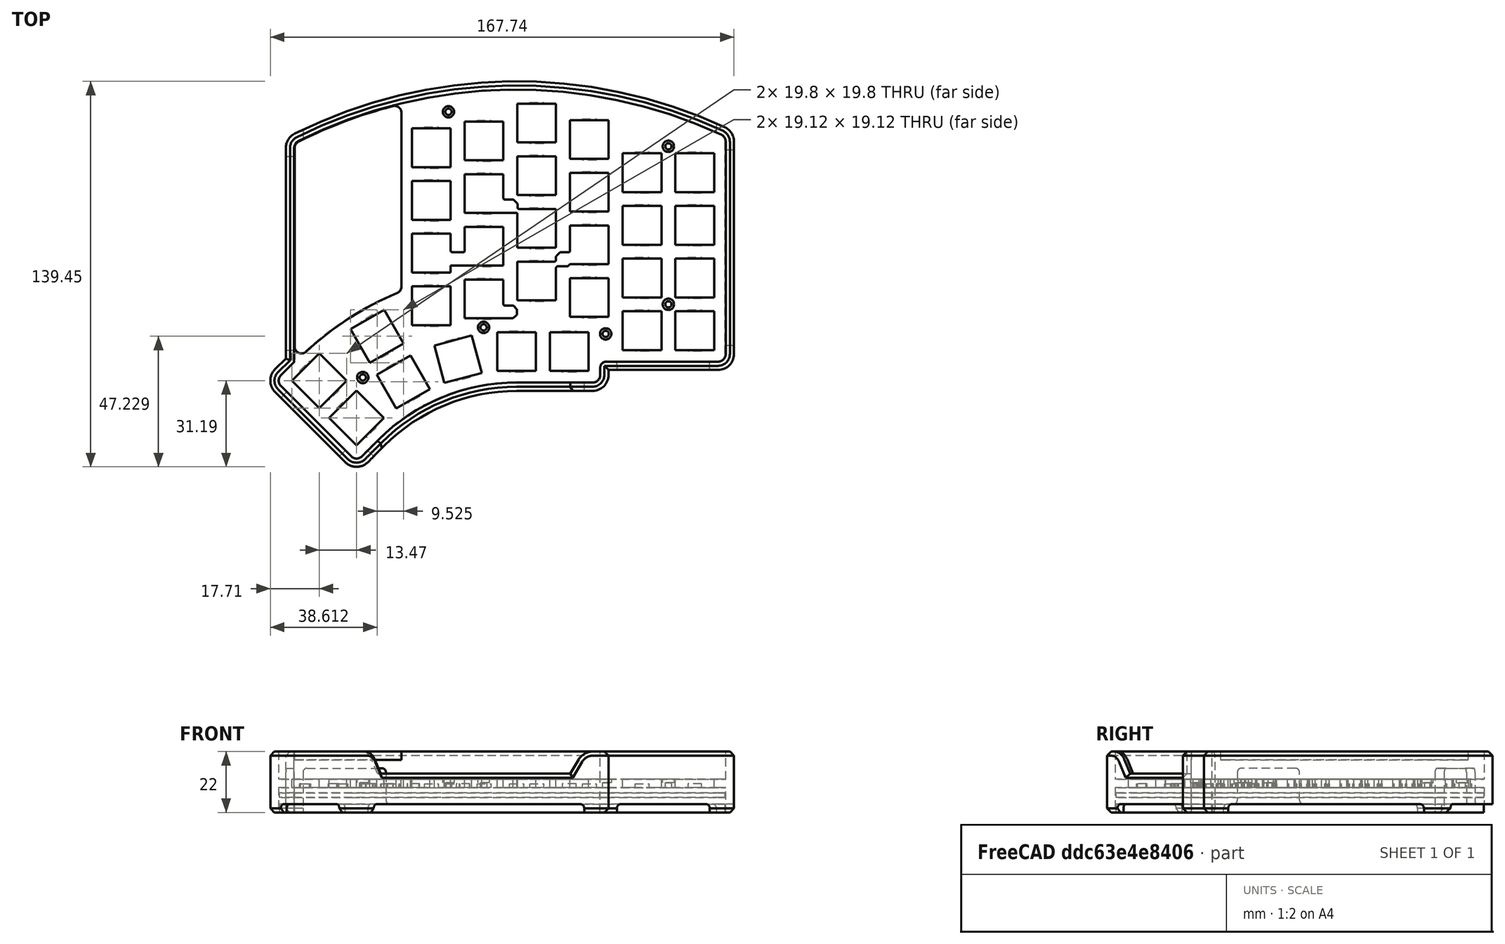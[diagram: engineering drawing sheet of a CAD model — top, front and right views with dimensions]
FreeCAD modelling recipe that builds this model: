
FCSTD DOCUMENT  (FreeCAD 1.1R38728 (Git))
Label: Elora3DPrintedCase
License: All rights reserved
LicenseURL: https://en.wikipedia.org/wiki/All_rights_reserved
objects: Sketcher::SketchObject×15, PartDesign::Pocket×12, PartDesign::Pad×7, Part::Feature×4, PartDesign::SubShapeBinder×4, PartDesign::Body×4, Part::Part2DObjectPython×1, Mesh::Feature×1, PartDesign::Chamfer×1
note: 103 computed .brp shape members not serialized (recipe doc carries the construction recipe); baked Part::Feature solids carry a one-line shape summary decoded from their .brp

FEATURE [Part::Feature] Polyline  label="Bottom Plate  - Shape"
  shape: bbox 161.3 x 133 x 2e-07 mm, 0 faces, 0 solids (baked)
FEATURE [Part::Part2DObjectPython] Block  label="Bottom Plate - Screw holes"  # Draft 2D object (typed FeaturePython)
FEATURE [PartDesign::SubShapeBinder] Binder
  BindCopyOnChange = 0
  BindMode = 0
  ClaimChildren = false
  Context = -> Body001 [Binder.]
  Fuse = false
  MakeFace = true
  OffsetFill = false
  OffsetIntersection = false
  OffsetJoinType = 0
  OffsetOpenResult = false
  PartialLoad = false
  Refine = true
  Relative = true
  Support = -> [Polyline]
  _Version = 2
FEATURE [PartDesign::Pad] Pad001
  Direction = (0,0,1)
  Length = 3
  Length2 = 10
  Profile = -> Binder
  Refine = true
  Suppressed = false
  Type = 0
FEATURE [PartDesign::Body] Body001  label="Bottom Plate"
  AllowCompound = false
  Group = -> [Binder,Pad001]
  Origin = -> Origin001
  Tip = -> Pad001
FEATURE [Part::Feature] Polyline002  label="Top Plate - Shape"
  shape: bbox 161.3 x 133 x 2e-07 mm, 0 faces, 0 solids (baked)
FEATURE [Part::Feature] Compound  label="Top Plate - Switch + Screw holes"
  shape: bbox 152.7 x 123.6 x 2e-07 mm, 34 faces, 0 solids (baked)
FEATURE [PartDesign::SubShapeBinder] Binder001
  BindCopyOnChange = 0
  BindMode = 0
  ClaimChildren = false
  Context = -> Body002 [Binder001.]
  Fuse = false
  MakeFace = true
  OffsetFill = false
  OffsetIntersection = false
  OffsetJoinType = 0
  OffsetOpenResult = false
  PartialLoad = false
  Placement = pos=(0,0,5.4) rot=(0,0,1;0rad)
  Refine = true
  Relative = true
  Support = -> [Polyline]
  _Version = 2
FEATURE [PartDesign::Pad] Pad003
  Direction = (0,0,1)
  Length = 1.6
  Length2 = 10
  Placement = pos=(0,0,5.4) rot=(0,0,1;0rad)
  Profile = -> Binder001
  Refine = true
  Suppressed = false
  Type = 0
FEATURE [PartDesign::Body] Body002  label="PCB"
  AllowCompound = false
  Group = -> [Binder001,Pad003]
  Origin = -> Origin002
  Tip = -> Pad003
FEATURE [Part::Feature] Polyline003  label="OLED Cover - Shape"
  shape: bbox 38.64 x 89.53 x 2e-07 mm, 0 faces, 0 solids (baked)
FEATURE [PartDesign::SubShapeBinder] Binder002
  BindCopyOnChange = 0
  BindMode = 0
  ClaimChildren = false
  Context = -> Body003 [Binder002.]
  Fuse = false
  MakeFace = true
  OffsetFill = false
  OffsetIntersection = false
  OffsetJoinType = 0
  OffsetOpenResult = false
  PartialLoad = false
  Placement = pos=(0,0,19) rot=(0,0,1;0rad)
  Refine = true
  Relative = true
  Support = -> [Polyline003]
  _Version = 2
FEATURE [PartDesign::Pad] Pad005
  Direction = (0,0,1)
  Length = 3
  Length2 = 10
  Placement = pos=(0,0,19) rot=(0,0,1;0rad)
  Profile = -> Binder002
  Refine = true
  Suppressed = false
  Type = 0
FEATURE [PartDesign::Body] Body003  label="OLED Cover"
  AllowCompound = false
  Group = -> [Binder002,Pad005]
  Origin = -> Origin003
  Tip = -> Pad005
FEATURE [Sketcher::SketchObject] Sketch
  ArcFitTolerance = 1e-06
  AttachmentSupport = -> [XY_Plane]
  FullyConstrained = true
  MakeInternals = false
  MapMode = 5
  sketch-geometry (33):
    g0: LineSegment StartX=119.09 StartY=-24.9948 StartZ=0 EndX=119.09 EndY=-22.425 EndZ=0
    g1: ArcOfCircle CenterX=121.29 CenterY=-22.425 CenterZ=0 NormalX=0 NormalY=0 NormalZ=1 AngleXU=-3.14159 Radius=2.2 StartAngle=4.71239 EndAngle=6.28319
    g2: LineSegment StartX=121.29 StartY=-20.225 StartZ=0 EndX=161.676 EndY=-20.225 EndZ=0
    g3: ArcOfCircle CenterX=161.676 CenterY=-17.425 CenterZ=0 NormalX=0 NormalY=0 NormalZ=1 AngleXU=0 Radius=2.8 StartAngle=4.71239 EndAngle=6.28319
    g4: LineSegment StartX=164.476 StartY=-17.425 StartZ=0 EndX=164.476 EndY=59.3777 EndZ=0
    g5: ArcOfCircle CenterX=161.676 CenterY=59.3777 CenterZ=0 NormalX=0 NormalY=0 NormalZ=1 AngleXU=0 Radius=2.8 StartAngle=-3.6e-15 EndAngle=1.13828
    g6: ArcOfCircle CenterX=88.8147 CenterY=-98.4444 CenterZ=0 NormalX=0 NormalY=0 NormalZ=1 AngleXU=0 Radius=176.629 StartAngle=1.13828 EndAngle=2.03404
    g7: ArcOfCircle CenterX=11.1386 CenterY=57.0643 CenterZ=0 NormalX=0 NormalY=0 NormalZ=1 AngleXU=0 Radius=2.8 StartAngle=2.03404 EndAngle=3.14159
    g8: LineSegment StartX=8.33865 StartY=57.0643 StartZ=0 EndX=8.33865 EndY=-20.317 EndZ=0
    g9: LineSegment StartX=8.33865 StartY=-20.317 StartZ=0 EndX=3.55563 EndY=-25.1 EndZ=0
    g10: ArcOfCircle CenterX=5.53553 CenterY=-27.0799 CenterZ=0 NormalX=0 NormalY=0 NormalZ=1 AngleXU=0 Radius=2.8 StartAngle=2.35619 EndAngle=3.92699
    g11: LineSegment StartX=3.55563 StartY=-29.0598 StartZ=0 EndX=28.9408 EndY=-54.445 EndZ=0
    g12: ArcOfCircle CenterX=30.9207 CenterY=-52.4651 CenterZ=0 NormalX=0 NormalY=0 NormalZ=1 AngleXU=0 Radius=2.8 StartAngle=3.92699 EndAngle=5.49779
    g13: LineSegment StartX=32.9006 StartY=-54.445 StartZ=0 EndX=38.8579 EndY=-48.4876 EndZ=0
    g14: ArcOfCircle CenterX=88.8147 CenterY=-98.4444 CenterZ=0 NormalX=0 NormalY=0 NormalZ=1 AngleXU=-3.14159 Radius=70.6496 StartAngle=4.71239 EndAngle=5.49779
    g15: LineSegment StartX=88.8147 StartY=-27.7948 StartZ=0 EndX=116.29 EndY=-27.7948 EndZ=0
    g16: ArcOfCircle CenterX=116.29 CenterY=-24.9948 CenterZ=0 NormalX=0 NormalY=0 NormalZ=1 AngleXU=0 Radius=2.8 StartAngle=4.71239 EndAngle=6.28319
    g17: ArcOfCircle CenterX=116.29 CenterY=-24.9948 CenterZ=0 NormalX=0 NormalY=0 NormalZ=1 AngleXU=0 Radius=5.8 StartAngle=4.71239 EndAngle=6.28319
    g18: LineSegment StartX=122.09 StartY=-24.9948 StartZ=0 EndX=122.09 EndY=-23.225 EndZ=0
    g19: LineSegment StartX=122.09 StartY=-23.225 StartZ=0 EndX=161.676 EndY=-23.225 EndZ=0
    g20: ArcOfCircle CenterX=161.676 CenterY=-17.425 CenterZ=0 NormalX=0 NormalY=0 NormalZ=1 AngleXU=0 Radius=5.8 StartAngle=4.71239 EndAngle=6.28319
    g21: LineSegment StartX=167.476 StartY=-17.425 StartZ=0 EndX=167.476 EndY=59.3777 EndZ=0
    g22: ArcOfCircle CenterX=161.676 CenterY=59.3777 CenterZ=0 NormalX=0 NormalY=0 NormalZ=1 AngleXU=0 Radius=5.8 StartAngle=-3.6e-15 EndAngle=1.13828
    g23: ArcOfCircle CenterX=88.8147 CenterY=-98.4444 CenterZ=0 NormalX=0 NormalY=0 NormalZ=1 AngleXU=0 Radius=179.629 StartAngle=1.13828 EndAngle=2.03404
    g24: ArcOfCircle CenterX=11.1386 CenterY=57.0643 CenterZ=0 NormalX=0 NormalY=0 NormalZ=1 AngleXU=0 Radius=5.8 StartAngle=2.03404 EndAngle=3.14159
    g25: LineSegment StartX=5.33865 StartY=57.0643 StartZ=0 EndX=5.33865 EndY=-19.0744 EndZ=0
    g26: LineSegment StartX=5.33865 StartY=-19.0744 StartZ=0 EndX=1.43431 EndY=-22.9787 EndZ=0
    g27: ArcOfCircle CenterX=5.53553 CenterY=-27.0799 CenterZ=0 NormalX=0 NormalY=0 NormalZ=1 AngleXU=0 Radius=5.8 StartAngle=2.35619 EndAngle=3.92699
    g28: LineSegment StartX=1.43431 StartY=-31.1812 StartZ=0 EndX=26.8194 EndY=-56.5663 EndZ=0
    g29: ArcOfCircle CenterX=30.9207 CenterY=-52.4651 CenterZ=0 NormalX=0 NormalY=0 NormalZ=1 AngleXU=0 Radius=5.8 StartAngle=3.92699 EndAngle=5.49779
    g30: LineSegment StartX=35.0219 StartY=-56.5663 StartZ=0 EndX=40.9793 EndY=-50.6089 EndZ=0
    g31: ArcOfCircle CenterX=88.8147 CenterY=-98.4444 CenterZ=0 NormalX=0 NormalY=0 NormalZ=1 AngleXU=-3.14159 Radius=67.6496 StartAngle=4.71239 EndAngle=5.49779
    g32: LineSegment StartX=88.8147 StartY=-30.7948 StartZ=0 EndX=116.29 EndY=-30.7948 EndZ=0
  constraints (66):
    c: Coincident(g13,g14)
    c: Coincident(g12,g13)
    c: Coincident(g11,g12)
    c: Coincident(g10,g11)
    c: Coincident(g9,g10)
    c: Coincident(g8,g9)
    c: Coincident(g7,g8)
    c: Coincident(g6,g7)
    c: Coincident(g5,g6)
    c: Coincident(g4,g5)
    c: Coincident(g3,g4)
    c: Coincident(g2,g3)
    c: Coincident(g1,g2)
    c: Coincident(g0,g1)
    c: Coincident(g0,g16)
    c: Coincident(g15,g16)
    c: Coincident(g14,g15)
    c: Block(g8)
    c: Block(g7)
    c: Block(g6)
    c: Block(g5)
    c: Block(g4)
    c: Block(g3)
    c: Block(g2)
    c: Block(g1)
    c: Block(g0)
    c: Block(g16)
    c: Block(g15)
    c: Block(g14)
    c: Block(g13)
    c: Block(g12)
    c: Block(g11)
    c: Block(g10)
    c: Block(g9)
    c: Coincident(g30,g31)
    c: Coincident(g29,g30)
    c: Coincident(g28,g29)
    c: Coincident(g27,g28)
    c: Coincident(g26,g27)
    c: Coincident(g25,g26)
    c: Coincident(g24,g25)
    c: Coincident(g23,g24)
    c: Coincident(g22,g23)
    c: Coincident(g21,g22)
    c: Coincident(g20,g21)
    c: Coincident(g19,g20)
    c: Coincident(g18,g19)
    c: Coincident(g17,g18)
    c: Coincident(g17,g32)
    c: Coincident(g31,g32)
    c: Block(g29)
    c: Block(g30)
    c: Block(g28)
    c: Block(g31)
    c: Block(g32)
    c: Block(g17)
    c: Block(g18)
    c: Block(g19)
    c: Block(g20)
    c: Block(g21)
    c: Block(g22)
    c: Block(g23)
    c: Block(g24)
    c: Block(g25)
    c: Block(g26)
    c: Block(g27)
FEATURE [PartDesign::Pad] Pad
  Direction = (0,0,1)
  Length = 22
  Length2 = 10
  Profile = -> Sketch
  ReferenceAxis = -> Sketch [N_Axis]
  Refine = true
  Suppressed = false
  Type = 0
FEATURE [PartDesign::SubShapeBinder] Binder003
  BindCopyOnChange = 0
  BindMode = 0
  ClaimChildren = false
  Context = -> Body [Binder003.]
  Fuse = false
  MakeFace = true
  OffsetFill = false
  OffsetIntersection = false
  OffsetJoinType = 0
  OffsetOpenResult = false
  PartialLoad = false
  Refine = true
  Relative = true
  Support = -> [Compound]
  _Version = 2
FEATURE [Mesh::Feature] switch_mx
  Placement = pos=(58,0,25.12) rot=(0,0,1;0rad)
FEATURE [Sketcher::SketchObject] Sketch015
  ArcFitTolerance = 1e-06
  AttachmentOffset = pos=(0,0,9) rot=(0,0,1;0rad)
  AttachmentSupport = -> [XY_Plane]
  ExternalGeometry = -> [Pad]
  FullyConstrained = true
  MakeInternals = false
  MapMode = 5
  Placement = pos=(0,0,9) rot=(0,0,1;0rad)
  sketch-geometry (28):
    g0: LineSegment StartX=46.9754 StartY=69.9449 StartZ=0 EndX=46.9754 EndY=7.07869 EndZ=0
    g1: ArcOfCircle CenterX=44.4754 CenterY=7.07869 CenterZ=0 NormalX=0 NormalY=0 NormalZ=1 AngleXU=-3.14159 Radius=2.5 StartAngle=1.96856 EndAngle=3.14159
    g2: ArcOfCircle CenterX=88.8147 CenterY=-98.4444 CenterZ=0 NormalX=0 NormalY=0 NormalZ=1 AngleXU=0 Radius=111.96 StartAngle=1.96858 EndAngle=2.32028
    g3: ArcOfCircle CenterX=44.4754 CenterY=69.9449 CenterZ=0 NormalX=0 NormalY=0 NormalZ=1 AngleXU=0 Radius=2.5 StartAngle=7e-16 EndAngle=1.82736
    g4: LineSegment [constr] StartX=44.4754 StartY=69.9449 StartZ=0 EndX=43.841 EndY=72.3631 EndZ=0
    g5: LineSegment [constr] StartX=44.4754 StartY=69.9449 StartZ=0 EndX=46.9754 EndY=69.9449 EndZ=0
    g6: LineSegment StartX=1.57574 StartY=-27.0799 StartZ=0 EndX=8.33865 EndY=-20.317 EndZ=0
    g7: LineSegment StartX=8.33865 StartY=-20.317 StartZ=0 EndX=8.33865 EndY=-14.654 EndZ=0
    g8: ArcOfCircle CenterX=10.8386 CenterY=-14.654 CenterZ=0 NormalX=0 NormalY=0 NormalZ=1 AngleXU=0 Radius=2.5 StartAngle=3.14159 EndAngle=5.46114
    g9: LineSegment [constr] StartX=8.33865 StartY=-14.654 StartZ=0 EndX=10.8386 EndY=-14.654 EndZ=0
    g10: LineSegment [constr] StartX=10.8386 StartY=-14.654 StartZ=0 EndX=12.5405 EndY=-16.4854 EndZ=0
    g11: LineSegment StartX=164.476 StartY=62.903 StartZ=0 EndX=164.476 EndY=-20.225 EndZ=0
    g12: LineSegment StartX=164.476 StartY=-20.225 StartZ=0 EndX=121.29 EndY=-20.225 EndZ=0
    g13: LineSegment StartX=119.09 StartY=-22.425 StartZ=0 EndX=119.09 EndY=-27.7948 EndZ=0
    g14: LineSegment StartX=119.09 StartY=-27.7948 StartZ=0 EndX=88.8147 EndY=-27.7948 EndZ=0
    g15: LineSegment StartX=38.8579 StartY=-48.4876 StartZ=0 EndX=30.9207 EndY=-56.4249 EndZ=0
    g16: LineSegment StartX=30.9207 StartY=-56.4249 StartZ=0 EndX=1.57574 EndY=-27.0799 EndZ=0
    g17: LineSegment StartX=119.09 StartY=-22.425 StartZ=0 EndX=121.29 EndY=-20.225 EndZ=0
    g18: LineSegment StartX=38.8579 StartY=-48.4876 StartZ=0 EndX=62.036 EndY=-33.7948 EndZ=0
    g19: LineSegment StartX=62.036 StartY=-33.7948 StartZ=0 EndX=88.8147 EndY=-27.7948 EndZ=0
    g20: LineSegment [constr] StartX=44.4754 StartY=7.07869 StartZ=0 EndX=46.9754 EndY=7.07869 EndZ=0
    g21: LineSegment [constr] StartX=44.4754 StartY=7.07869 StartZ=0 EndX=45.4438 EndY=4.77386 EndZ=0
    g22: LineSegment StartX=43.841 StartY=73.8631 StartZ=0 EndX=68.104 EndY=78.4766 EndZ=0
    g23: LineSegment StartX=68.104 StartY=78.4766 StartZ=0 EndX=92.7743 EndY=79.6406 EndZ=0
    g24: LineSegment StartX=92.7743 StartY=79.6406 StartZ=0 EndX=117.368 EndY=77.3812 EndZ=0
    g25: LineSegment StartX=117.368 StartY=77.3812 StartZ=0 EndX=141.414 EndY=71.7417 EndZ=0
    g26: LineSegment StartX=141.414 StartY=71.7417 StartZ=0 EndX=164.476 EndY=62.903 EndZ=0
    g27: LineSegment StartX=43.841 StartY=72.3631 StartZ=0 EndX=43.841 EndY=73.8631 EndZ=0
  constraints (76):
    c: PointOnObject(g6,g-4)
    c: Coincident(g0,g1)
    c: Coincident(g1,g2)
    c: Vertical(g0)
    c: Coincident(g3,g0)
    c: Radius(g3) = 2.5
    c: Coincident(g4,g3)
    c: Coincident(g5,g3)
    c: Coincident(g5,g0)
    c: Angle(g5,g0) = 1.5708
    c: Angle(g5,g4) = 1.82736
    c: Coincident(g6,g-5)
    c: Coincident(g7,g6)
    c: PointOnObject(g7,g-5)
    c: Radius(g2) = 111.96
    c: Radius(g1) = 2.5
    c: DistanceY(g0,g0) = 62.8662
    c: Coincident(g8,g7)
    c: Coincident(g8,g2)
    c: Coincident(g9,g7)
    c: Coincident(g9,g8)
    c: Coincident(g10,g8)
    c: Coincident(g10,g2)
    c: Angle(g9,g7) = 1.5708
    c: Angle(g9,g10) = 2.31954
    c: Radius(g8) = 2.5
    c: PointOnObject(g3,g-3)
    c: Coincident(g12,g-10)
    c: Coincident(g13,g-9)
    c: Coincident(g14,g-8)
    c: Coincident(g15,g-7)
    c: PointOnObject(g-6,g16)
    c: Coincident(g6,g16)
    c: PointOnObject(g-7,g15)
    c: PointOnObject(g-6,g16)
    c: Coincident(g15,g16)
    c: Coincident(g13,g14)
    c: PointOnObject(g-8,g14)
    c: PointOnObject(g-9,g13)
    c: Coincident(g17,g13)
    c: Coincident(g17,g12)
    c: Coincident(g11,g12)
    c: PointOnObject(g-10,g12)
    c: PointOnObject(g-11,g11)
    c: PointOnObject(g-11,g11)
    c: Coincident(g18,g15)
    c: Coincident(g19,g18)
    c: Coincident(g19,g14)
    c: Equal(g19,g18)
    c: DistanceY(g18,g14) = 6
    c: Coincident(g2,g-3)
    c: Coincident(g20,g1)
    c: Coincident(g20,g0)
    c: Horizontal(g20)
    c: Coincident(g21,g1)
    c: Coincident(g21,g1)
    c: Angle(g21,g20) = 1.17304
    c: Coincident(g23,g22)
    c: Coincident(g24,g23)
    c: Coincident(g25,g24)
    c: Coincident(g26,g25)
    c: Equal(g23,g24)
    c: Equal(g24,g25)
    c: Equal(g25,g26)
    c: Coincident(g26,g11)
    c: Equal(g22,g23)
    c: Distance(g22,g-3) = 1.5
    c: Distance(g23,g-3) = 1.5
    c: Distance(g24,g-3) = 1.5
    c: Distance(g25,g-3) = 1.5
    c: Coincident(g3,g4)
    c: Coincident(g27,g3)
    c: Vertical(g27)
    c: Coincident(g27,g22)
    c: DistanceY(g27,g27) = 1.5
    c: Distance(g-3,g26) = 1.5
FEATURE [PartDesign::Pad] Pad009
  BaseFeature = -> Pad
  Direction = (0,0,1)
  Length = 3
  Length2 = 10
  Profile = -> Sketch015
  ReferenceAxis = -> Sketch015 [N_Axis]
  Refine = true
  Suppressed = false
  Type = 0
FEATURE [Sketcher::SketchObject] Sketch002
  ArcFitTolerance = 1e-06
  AttachmentOffset = pos=(0,0,-90) rot=(0,0,1;0rad)
  AttachmentSupport = -> [XZ_Plane]
  ExternalGeometry = -> [Pad009]
  FullyConstrained = true
  MakeInternals = false
  MapMode = 5
  Placement = pos=(0,90,-2e-14) rot=(1,0,0;1.5708rad)
  sketch-geometry (14):
    g0: LineSegment StartX=161.107 StartY=0 StartZ=0 EndX=161.107 EndY=1.5 EndZ=0
    g1: LineSegment StartX=159.607 StartY=3 StartZ=0 EndX=43.0469 EndY=3 EndZ=0
    g2: LineSegment StartX=11.5469 StartY=14.5 StartZ=0 EndX=11.5469 EndY=0 EndZ=0
    g3: LineSegment StartX=11.5469 StartY=0 StartZ=0 EndX=161.107 EndY=0 EndZ=0
    g4: LineSegment StartX=13.0469 StartY=16 StartZ=0 EndX=40.0469 EndY=16 EndZ=0
    g5: LineSegment StartX=41.5469 StartY=14.5 StartZ=0 EndX=41.5469 EndY=4.5 EndZ=0
    g6: ArcOfCircle CenterX=159.607 CenterY=1.5 CenterZ=0 NormalX=0 NormalY=0 NormalZ=1 AngleXU=0 Radius=1.5 StartAngle=0 EndAngle=1.5708
    g7: GeomPoint [constr] X=161.107 Y=3 Z=0
    g8: ArcOfCircle CenterX=43.0469 CenterY=4.5 CenterZ=0 NormalX=0 NormalY=0 NormalZ=1 AngleXU=0 Radius=1.5 StartAngle=3.14159 EndAngle=4.71239
    g9: GeomPoint [constr] X=41.5469 Y=3 Z=0
    g10: ArcOfCircle CenterX=40.0469 CenterY=14.5 CenterZ=0 NormalX=0 NormalY=0 NormalZ=1 AngleXU=0 Radius=1.5 StartAngle=-9e-16 EndAngle=1.5708
    g11: GeomPoint [constr] X=41.5469 Y=16 Z=0
    g12: ArcOfCircle CenterX=13.0469 CenterY=14.5 CenterZ=0 NormalX=0 NormalY=0 NormalZ=1 AngleXU=0 Radius=1.5 StartAngle=1.5708 EndAngle=3.14159
    g13: GeomPoint [constr] X=11.5469 Y=16 Z=0
  constraints (34):
    c: Coincident(g2,g3)
    c: Coincident(g3,g0)
    c: Vertical(g0)
    c: Vertical(g2)
    c: Horizontal(g1)
    c: Horizontal(g3)
    c: Distance(g7,g3) = 3
    c: PointOnObject(g0,g-1)
    c: Distance(g13,g11) = 30
    c: Horizontal(g4)
    c: Vertical(g5)
    c: PointOnObject(g7,g0)
    c: PointOnObject(g7,g1)
    c: Tangent(g0,g6) = -1.5708
    c: Tangent(g1,g6) = -1.5708
    c: Radius(g6) = 1.5
    c: PointOnObject(g9,g1)
    c: PointOnObject(g9,g5)
    c: Tangent(g1,g8) = 1.5708
    c: Tangent(g5,g8) = -1.5708
    c: PointOnObject(g11,g5)
    c: PointOnObject(g11,g4)
    c: Tangent(g5,g10) = 1.5708
    c: Tangent(g4,g10) = 1.5708
    c: PointOnObject(g13,g4)
    c: PointOnObject(g13,g2)
    c: Tangent(g4,g12) = 1.5708
    c: Tangent(g2,g12) = -1.5708
    c: Equal(g6,g8)
    c: Equal(g8,g10)
    c: Equal(g10,g12)
    c: DistanceX(g0,g-4) = 3
    c: DistanceX(g-3,g2) = 3
    c: DistanceY(g13,g-3) = 6
FEATURE [Sketcher::SketchObject] Sketch003
  ArcFitTolerance = 1e-06
  AttachmentSupport = -> [Pad009]
  ExternalGeometry = -> [Pad009]
  FullyConstrained = true
  MakeInternals = false
  MapMode = 5
  Placement = pos=(167.476,-5.577e-13,0) rot=(0.57735,0.57735,0.57735;2.0944rad)
  sketch-geometry (8):
    g0: LineSegment StartX=-14.425 StartY=0 StartZ=0 EndX=56.3777 EndY=0 EndZ=0
    g1: LineSegment StartX=56.3777 StartY=0 StartZ=0 EndX=56.3777 EndY=1.5 EndZ=0
    g2: LineSegment StartX=54.8777 StartY=3 StartZ=0 EndX=-12.925 EndY=3 EndZ=0
    g3: LineSegment StartX=-14.425 StartY=1.5 StartZ=0 EndX=-14.425 EndY=0 EndZ=0
    g4: ArcOfCircle CenterX=-12.925 CenterY=1.5 CenterZ=0 NormalX=0 NormalY=0 NormalZ=1 AngleXU=0 Radius=1.5 StartAngle=1.5708 EndAngle=3.14159
    g5: GeomPoint [constr] X=-14.425 Y=3 Z=0
    g6: ArcOfCircle CenterX=54.8777 CenterY=1.5 CenterZ=0 NormalX=0 NormalY=0 NormalZ=1 AngleXU=0 Radius=1.5 StartAngle=2.54e-14 EndAngle=1.5708
    g7: GeomPoint [constr] X=56.3777 Y=3 Z=0
  constraints (20):
    c: Coincident(g0,g1)
    c: Coincident(g3,g0)
    c: Horizontal(g0)
    c: Horizontal(g2)
    c: Vertical(g1)
    c: Vertical(g3)
    c: PointOnObject(g0,g-1)
    c: DistanceY(g3,g5) = 3
    c: PointOnObject(g5,g3)
    c: PointOnObject(g5,g2)
    c: Tangent(g3,g4) = -1.5708
    c: Tangent(g2,g4) = -1.5708
    c: PointOnObject(g7,g2)
    c: PointOnObject(g7,g1)
    c: Tangent(g2,g6) = -1.5708
    c: Tangent(g1,g6) = -1.5708
    c: Radius(g4) = 1.5
    c: Equal(g4,g6)
    c: DistanceX(g0,g-4) = 3
    c: DistanceX(g-3,g0) = 3
FEATURE [Sketcher::SketchObject] Sketch004
  ArcFitTolerance = 1e-06
  AttachmentSupport = -> [Pad009]
  ExternalGeometry = -> [Pad009]
  FullyConstrained = true
  MakeInternals = false
  MapMode = 5
  Placement = pos=(-5.41e-14,-23.225,0) rot=(1,0,0;1.5708rad)
  sketch-geometry (8):
    g0: LineSegment StartX=125.09 StartY=0 StartZ=0 EndX=158.676 EndY=0 EndZ=0
    g1: LineSegment StartX=158.676 StartY=0 StartZ=0 EndX=158.676 EndY=1.5 EndZ=0
    g2: LineSegment StartX=157.176 StartY=3 StartZ=0 EndX=126.59 EndY=3 EndZ=0
    g3: LineSegment StartX=125.09 StartY=1.5 StartZ=0 EndX=125.09 EndY=0 EndZ=0
    g4: ArcOfCircle CenterX=126.59 CenterY=1.5 CenterZ=0 NormalX=0 NormalY=0 NormalZ=1 AngleXU=0 Radius=1.5 StartAngle=1.5708 EndAngle=3.14159
    g5: GeomPoint [constr] X=125.09 Y=3 Z=0
    g6: ArcOfCircle CenterX=157.176 CenterY=1.5 CenterZ=0 NormalX=0 NormalY=0 NormalZ=1 AngleXU=0 Radius=1.5 StartAngle=1.5e-15 EndAngle=1.5708
    g7: GeomPoint [constr] X=158.676 Y=3 Z=0
  constraints (20):
    c: Coincident(g0,g1)
    c: Coincident(g3,g0)
    c: Horizontal(g0)
    c: Horizontal(g2)
    c: Vertical(g1)
    c: Vertical(g3)
    c: PointOnObject(g0,g-1)
    c: DistanceY(g1,g7) = 3
    c: PointOnObject(g5,g3)
    c: PointOnObject(g5,g2)
    c: Tangent(g3,g4) = -1.5708
    c: Tangent(g2,g4) = -1.5708
    c: PointOnObject(g7,g2)
    c: PointOnObject(g7,g1)
    c: Tangent(g2,g6) = -1.5708
    c: Tangent(g1,g6) = -1.5708
    c: Radius(g4) = 1.5
    c: Equal(g4,g6)
    c: DistanceX(g0,g-4) = 3
    c: DistanceX(g-3,g0) = 3
FEATURE [Sketcher::SketchObject] Sketch005
  ArcFitTolerance = 1e-06
  AttachmentSupport = -> [Pad009]
  ExternalGeometry = -> [Pad009]
  FullyConstrained = true
  MakeInternals = false
  MapMode = 5
  Placement = pos=(-1.195e-13,-30.7948,0) rot=(1,0,0;1.5708rad)
  sketch-geometry (6):
    g0: LineSegment StartX=88.8147 StartY=0 StartZ=0 EndX=113.29 EndY=0 EndZ=0
    g1: LineSegment StartX=113.29 StartY=0 StartZ=0 EndX=113.29 EndY=1.5 EndZ=0
    g2: LineSegment StartX=111.79 StartY=3 StartZ=0 EndX=88.8147 EndY=3 EndZ=0
    g3: LineSegment StartX=88.8147 StartY=3 StartZ=0 EndX=88.8147 EndY=0 EndZ=0
    g4: ArcOfCircle CenterX=111.79 CenterY=1.5 CenterZ=0 NormalX=0 NormalY=0 NormalZ=1 AngleXU=0 Radius=1.5 StartAngle=1e-16 EndAngle=1.5708
    g5: GeomPoint [constr] X=113.29 Y=3 Z=0
  constraints (16):
    c: Coincident(g0,g1)
    c: Coincident(g2,g3)
    c: Coincident(g3,g0)
    c: Horizontal(g0)
    c: Horizontal(g2)
    c: Vertical(g1)
    c: Vertical(g3)
    c: Distance(g0,g2) = 3
    c: PointOnObject(g5,g2)
    c: PointOnObject(g5,g1)
    c: Tangent(g2,g4) = -1.5708
    c: Tangent(g1,g4) = -1.5708
    c: Radius(g4) = 1.5
    c: PointOnObject(g2,g-3)
    c: DistanceX(g0,g-4) = 3
    c: PointOnObject(g0,g-1)
FEATURE [Sketcher::SketchObject] Sketch006
  ArcFitTolerance = 1e-06
  AttachmentSupport = -> [Pad009]
  ExternalGeometry = -> [Pad009]
  FullyConstrained = true
  MakeInternals = false
  MapMode = 5
  Placement = pos=(45.7941,-45.7941,0) rot=(0.862856,0.357407,0.357407;1.71777rad)
  sketch-geometry (6):
    g0: LineSegment StartX=-6.8092 StartY=0 StartZ=0 EndX=-6.8092 EndY=3 EndZ=0
    g1: LineSegment StartX=-6.8092 StartY=3 StartZ=0 EndX=-10.7342 EndY=3 EndZ=0
    g2: LineSegment StartX=-12.2342 StartY=1.5 StartZ=0 EndX=-12.2342 EndY=0 EndZ=0
    g3: LineSegment StartX=-12.2342 StartY=0 StartZ=0 EndX=-6.8092 EndY=0 EndZ=0
    g4: ArcOfCircle CenterX=-10.7342 CenterY=1.5 CenterZ=0 NormalX=0 NormalY=0 NormalZ=1 AngleXU=0 Radius=1.5 StartAngle=1.5708 EndAngle=3.14159
    g5: GeomPoint [constr] X=-12.2342 Y=3 Z=0
  constraints (16):
    c: Coincident(g0,g1)
    c: Coincident(g2,g3)
    c: Coincident(g3,g0)
    c: Vertical(g0)
    c: Vertical(g2)
    c: Horizontal(g1)
    c: Horizontal(g3)
    c: Distance(g1,g3) = 3
    c: PointOnObject(g5,g2)
    c: PointOnObject(g5,g1)
    c: Tangent(g2,g4) = -1.5708
    c: Tangent(g1,g4) = -1.5708
    c: Radius(g4) = 1.5
    c: PointOnObject(g0,g-4)
    c: DistanceX(g-3,g2) = 3
    c: PointOnObject(g2,g-1)
FEATURE [Sketcher::SketchObject] Sketch007
  ArcFitTolerance = 1e-06
  AttachmentOffset = pos=(0,0,55) rot=(0,0,1;0rad)
  AttachmentSupport = -> [XZ_Plane]
  ExternalGeometry = -> [Sketch005]
  FullyConstrained = true
  MakeInternals = false
  MapMode = 5
  Placement = pos=(0,-55,1.22e-14) rot=(1,0,0;1.5708rad)
  sketch-geometry (4):
    g0: LineSegment StartX=38.8147 StartY=0 StartZ=0 EndX=90.8147 EndY=0 EndZ=0
    g1: LineSegment StartX=90.8147 StartY=0 StartZ=0 EndX=90.8147 EndY=3 EndZ=0
    g2: LineSegment StartX=90.8147 StartY=3 StartZ=0 EndX=38.8147 EndY=3 EndZ=0
    g3: LineSegment StartX=38.8147 StartY=3 StartZ=0 EndX=38.8147 EndY=0 EndZ=0
  constraints (12):
    c: Coincident(g0,g1)
    c: Coincident(g1,g2)
    c: Coincident(g2,g3)
    c: Coincident(g3,g0)
    c: Horizontal(g0)
    c: Horizontal(g2)
    c: Vertical(g1)
    c: Vertical(g3)
    c: Distance(g0,g2) = 3
    c: PointOnObject(g0,g-1)
    c: DistanceX(g0,g0) = 52
    c: DistanceX(g-3,g0) = 2
FEATURE [Sketcher::SketchObject] Sketch008
  ArcFitTolerance = 1e-06
  AttachmentSupport = -> [Pad009]
  ExternalGeometry = -> [Pad009]
  FullyConstrained = true
  MakeInternals = false
  MapMode = 5
  Placement = pos=(-14.8734,-14.8734,0) rot=(0.862856,-0.357407,-0.357407;1.71777rad)
  sketch-geometry (8):
    g0: LineSegment StartX=26.0626 StartY=0 StartZ=0 EndX=55.9626 EndY=0 EndZ=0
    g1: LineSegment StartX=55.9626 StartY=0 StartZ=0 EndX=55.9626 EndY=1.5 EndZ=0
    g2: LineSegment StartX=54.4626 StartY=3 StartZ=0 EndX=27.5626 EndY=3 EndZ=0
    g3: LineSegment StartX=26.0626 StartY=1.5 StartZ=0 EndX=26.0626 EndY=0 EndZ=0
    g4: ArcOfCircle CenterX=27.5626 CenterY=1.5 CenterZ=0 NormalX=0 NormalY=0 NormalZ=1 AngleXU=0 Radius=1.5 StartAngle=1.5708 EndAngle=3.14159
    g5: GeomPoint [constr] X=26.0626 Y=3 Z=0
    g6: ArcOfCircle CenterX=54.4626 CenterY=1.5 CenterZ=0 NormalX=0 NormalY=0 NormalZ=1 AngleXU=0 Radius=1.5 StartAngle=1e-16 EndAngle=1.5708
    g7: GeomPoint [constr] X=55.9626 Y=3 Z=0
  constraints (20):
    c: Coincident(g0,g1)
    c: Coincident(g3,g0)
    c: Horizontal(g0)
    c: Horizontal(g2)
    c: Vertical(g1)
    c: Vertical(g3)
    c: Distance(g0,g5) = 3
    c: PointOnObject(g0,g-1)
    c: PointOnObject(g5,g3)
    c: PointOnObject(g5,g2)
    c: Tangent(g3,g4) = -1.5708
    c: Tangent(g2,g4) = -1.5708
    c: PointOnObject(g7,g1)
    c: PointOnObject(g7,g2)
    c: Tangent(g1,g6) = -1.5708
    c: Tangent(g2,g6) = -1.5708
    c: Radius(g6) = 1.5
    c: Equal(g6,g4)
    c: DistanceX(g-3,g0) = 3
    c: DistanceX(g0,g-4) = 3
FEATURE [Sketcher::SketchObject] Sketch009
  ArcFitTolerance = 1e-06
  AttachmentSupport = -> [Pad009]
  ExternalGeometry = -> [Pad009]
  FullyConstrained = true
  MakeInternals = false
  MapMode = 5
  Placement = pos=(5.33865,2.51e-14,0) rot=(0.57735,-0.57735,-0.57735;2.0944rad)
  sketch-geometry (20):
    g0: LineSegment StartX=-54.0643 StartY=0 StartZ=0 EndX=16.0744 EndY=0 EndZ=0
    g1: LineSegment StartX=16.0744 StartY=0 StartZ=0 EndX=16.0744 EndY=1.5 EndZ=0
    g2: LineSegment StartX=-12.8756 StartY=3 StartZ=0 EndX=-52.5643 EndY=3 EndZ=0
    g3: LineSegment StartX=-54.0643 StartY=1.5 StartZ=0 EndX=-54.0643 EndY=0 EndZ=0
    g4: LineSegment StartX=14.5744 StartY=3 StartZ=0 EndX=12.6244 EndY=3 EndZ=0
    g5: LineSegment StartX=-11.3756 StartY=4.5 StartZ=0 EndX=-11.3756 EndY=14.5 EndZ=0
    g6: LineSegment StartX=-9.87561 StartY=16 StartZ=0 EndX=9.62439 EndY=16 EndZ=0
    g7: LineSegment StartX=11.1244 StartY=14.5 StartZ=0 EndX=11.1244 EndY=4.5 EndZ=0
    g8: ArcOfCircle CenterX=-52.5643 CenterY=1.5 CenterZ=0 NormalX=0 NormalY=0 NormalZ=1 AngleXU=0 Radius=1.5 StartAngle=1.5708 EndAngle=3.14159
    g9: GeomPoint [constr] X=-54.0643 Y=3 Z=0
    g10: ArcOfCircle CenterX=-12.8756 CenterY=4.5 CenterZ=0 NormalX=0 NormalY=0 NormalZ=1 AngleXU=0 Radius=1.5 StartAngle=4.71239 EndAngle=6.28319
    g11: GeomPoint [constr] X=-11.3756 Y=3 Z=0
    g12: ArcOfCircle CenterX=-9.87561 CenterY=14.5 CenterZ=0 NormalX=0 NormalY=0 NormalZ=1 AngleXU=0 Radius=1.5 StartAngle=1.5708 EndAngle=3.14159
    g13: GeomPoint [constr] X=-11.3756 Y=16 Z=0
    g14: ArcOfCircle CenterX=9.62439 CenterY=14.5 CenterZ=0 NormalX=0 NormalY=0 NormalZ=1 AngleXU=0 Radius=1.5 StartAngle=0 EndAngle=1.5708
    g15: GeomPoint [constr] X=11.1244 Y=16 Z=0
    g16: ArcOfCircle CenterX=12.6244 CenterY=4.5 CenterZ=0 NormalX=0 NormalY=0 NormalZ=1 AngleXU=0 Radius=1.5 StartAngle=3.14159 EndAngle=4.71239
    g17: GeomPoint [constr] X=11.1244 Y=3 Z=0
    g18: ArcOfCircle CenterX=14.5744 CenterY=1.5 CenterZ=0 NormalX=0 NormalY=0 NormalZ=1 AngleXU=0 Radius=1.5 StartAngle=0 EndAngle=1.5708
    g19: GeomPoint [constr] X=16.0744 Y=3 Z=0
  constraints (48):
    c: Coincident(g0,g1)
    c: Coincident(g3,g0)
    c: Horizontal(g0)
    c: Horizontal(g2)
    c: Vertical(g1)
    c: Vertical(g3)
    c: Distance(g0,g9) = 3
    c: PointOnObject(g0,g-1)
    c: Distance(g1,g19) = 3
    c: Horizontal(g4)
    c: DistanceX(g17,g19) = 4.95
    c: Vertical(g5)
    c: Horizontal(g6)
    c: Vertical(g7)
    c: DistanceX(g13,g15) = 22.5
    c: PointOnObject(g9,g3)
    c: PointOnObject(g9,g2)
    c: Tangent(g3,g8) = -1.5708
    c: Tangent(g2,g8) = -1.5708
    c: PointOnObject(g11,g2)
    c: PointOnObject(g11,g5)
    c: Tangent(g2,g10) = 1.5708
    c: Tangent(g5,g10) = -1.5708
    c: PointOnObject(g13,g5)
    c: PointOnObject(g13,g6)
    c: Tangent(g5,g12) = 1.5708
    c: Tangent(g6,g12) = 1.5708
    c: PointOnObject(g15,g6)
    c: PointOnObject(g15,g7)
    c: Tangent(g6,g14) = 1.5708
    c: Tangent(g7,g14) = 1.5708
    c: PointOnObject(g17,g7)
    c: PointOnObject(g17,g4)
    c: Tangent(g7,g16) = -1.5708
    c: Tangent(g4,g16) = 1.5708
    c: PointOnObject(g19,g4)
    c: PointOnObject(g19,g1)
    c: Tangent(g4,g18) = -1.5708
    c: Tangent(g1,g18) = -1.5708
    c: Radius(g8) = 1.5
    c: Equal(g8,g10)
    c: Equal(g10,g12)
    c: Equal(g12,g14)
    c: Equal(g14,g16)
    c: Equal(g16,g18)
    c: DistanceY(g15,g-4) = 6
    c: DistanceX(g0,g-4) = 3
    c: DistanceX(g-3,g0) = 3
FEATURE [PartDesign::Pocket] Pocket
  BaseFeature = -> Pad009
  Direction = (0,1,-2e-16)
  Length = 0
  Length2 = 5
  Profile = -> Sketch002
  ReferenceAxis = -> Sketch002 [N_Axis]
  Refine = true
  Suppressed = false
  Type = 3
  UpToFace = -> Pad009 [Face25]
FEATURE [PartDesign::Pocket] Pocket001
  BaseFeature = -> Pocket
  Direction = (-1,3.2e-15,1e-16)
  Length = 3
  Length2 = 5
  Profile = -> Sketch003
  ReferenceAxis = -> Sketch003 [N_Axis]
  Refine = true
  Suppressed = false
  Type = 0
FEATURE [PartDesign::Pocket] Pocket002
  BaseFeature = -> Pocket001
  Direction = (2.3e-15,1,-2e-16)
  Length = 3
  Length2 = 5
  Profile = -> Sketch004
  ReferenceAxis = -> Sketch004 [N_Axis]
  Refine = true
  Suppressed = false
  Type = 0
FEATURE [PartDesign::Pocket] Pocket003
  BaseFeature = -> Pocket002
  Direction = (3.9e-15,1,-2e-16)
  Length = 3
  Length2 = 5
  Profile = -> Sketch005
  ReferenceAxis = -> Sketch005 [N_Axis]
  Refine = true
  Suppressed = false
  Type = 0
FEATURE [PartDesign::Pocket] Pocket004
  BaseFeature = -> Pocket003
  Direction = (-0.707107,0.707107,0)
  Length = 3
  Length2 = 5
  Profile = -> Sketch006
  ReferenceAxis = -> Sketch006 [N_Axis]
  Refine = true
  Suppressed = false
  Type = 0
FEATURE [PartDesign::Pocket] Pocket005
  BaseFeature = -> Pocket004
  Direction = (0,1,-2e-16)
  Length = 0
  Length2 = 5
  Profile = -> Sketch007
  ReferenceAxis = -> Sketch007 [N_Axis]
  Refine = true
  Suppressed = false
  Type = 3
  UpToFace = -> Pocket004 [Face11]
FEATURE [PartDesign::Pocket] Pocket006
  BaseFeature = -> Pocket005
  Direction = (0.707107,0.707107,2e-16)
  Length = 3
  Length2 = 5
  Profile = -> Sketch008
  ReferenceAxis = -> Sketch008 [N_Axis]
  Refine = true
  Suppressed = false
  Type = 0
FEATURE [PartDesign::Pocket] Pocket007
  BaseFeature = -> Pocket006
  Direction = (1,4.6e-15,1e-16)
  Length = 3
  Length2 = 5
  Profile = -> Sketch009
  ReferenceAxis = -> Sketch009 [N_Axis]
  Refine = true
  Suppressed = false
  Type = 0
FEATURE [Sketcher::SketchObject] Sketch010
  ArcFitTolerance = 1e-06
  AttachmentSupport = -> [Pocket007]
  ExternalGeometry = -> [Pocket007]
  FullyConstrained = true
  MakeInternals = false
  MapMode = 5
  Placement = pos=(0,0,22) rot=(0,0,1;0rad)
  sketch-geometry (7):
    g0: LineSegment StartX=35.0219 StartY=-56.5663 StartZ=0 EndX=32.9006 EndY=-54.445 EndZ=0
    g1: LineSegment StartX=35.0219 StartY=-56.5663 StartZ=0 EndX=40.9793 EndY=-50.6089 EndZ=0
    g2: LineSegment StartX=40.9793 StartY=-50.6089 StartZ=0 EndX=88.8147 EndY=-30.7948 EndZ=0
    g3: LineSegment StartX=88.8147 StartY=-30.7948 StartZ=0 EndX=116.29 EndY=-30.7948 EndZ=0
    g4: LineSegment StartX=116.29 StartY=-30.7948 StartZ=0 EndX=116.29 EndY=-27.7948 EndZ=0
    g5: LineSegment StartX=116.29 StartY=-27.7948 StartZ=0 EndX=59.5507 EndY=-27.7948 EndZ=0
    g6: LineSegment StartX=32.9006 StartY=-54.445 StartZ=0 EndX=59.5507 EndY=-27.7948 EndZ=0
  constraints (17):
    c: PointOnObject(g0,g-6)
    c: Coincident(g1,g0)
    c: Coincident(g1,g-3)
    c: Coincident(g2,g1)
    c: Coincident(g2,g-4)
    c: Coincident(g3,g2)
    c: Coincident(g4,g3)
    c: PointOnObject(g4,g-5)
    c: Vertical(g4)
    c: Coincident(g5,g4)
    c: Horizontal(g5)
    c: Coincident(g6,g0)
    c: Coincident(g6,g5)
    c: PointOnObject(g-6,g6)
    c: Perpendicular(g1,g0)
    c: Coincident(g3,g-4)
    c: Coincident(g0,g-3)
FEATURE [PartDesign::Pocket] Pocket008
  BaseFeature = -> Pocket007
  Direction = (0,0,-1)
  Length = 8
  Length2 = 5
  Profile = -> Sketch010
  ReferenceAxis = -> Sketch010 [N_Axis]
  Refine = true
  Suppressed = false
  Type = 0
FEATURE [Sketcher::SketchObject] Sketch011
  ArcFitTolerance = 1e-06
  AttachmentSupport = -> [Pocket008]
  ExternalGeometry = -> [Pocket008]
  FullyConstrained = true
  MakeInternals = false
  MapMode = 5
  Placement = pos=(45.7941,-45.7941,0) rot=(0.862856,0.357407,0.357407;1.71777rad)
  sketch-geometry (4):
    g0: LineSegment StartX=-15.2342 StartY=22 StartZ=0 EndX=-15.2342 EndY=14 EndZ=0
    g1: LineSegment StartX=-15.2342 StartY=14 StartZ=0 EndX=-7.2342 EndY=14 EndZ=0
    g2: LineSegment StartX=-7.2342 StartY=14 StartZ=0 EndX=-10.2251 EndY=19.1239 EndZ=0
    g3: ArcOfCircle CenterX=-15.2342 CenterY=16.2 CenterZ=0 NormalX=0 NormalY=0 NormalZ=1 AngleXU=0 Radius=5.8 StartAngle=0.528364 EndAngle=1.5708
  constraints (10):
    c: Coincident(g2,g1)
    c: DistanceX(g1,g1) = 8
    c: Coincident(g0,g-3)
    c: Coincident(g0,g-4)
    c: Coincident(g1,g0)
    c: PointOnObject(g1,g-4)
    c: PointOnObject(g3,g0)
    c: Coincident(g3,g0)
    c: Radius(g3) = 5.8
    c: Tangent(g2,g3) = -1.5708
FEATURE [Sketcher::SketchObject] Sketch012
  ArcFitTolerance = 1e-06
  AttachmentSupport = -> [Pocket008]
  ExternalGeometry = -> [Pocket008]
  FullyConstrained = true
  MakeInternals = false
  MapMode = 5
  Placement = pos=(-1.195e-13,-30.7948,0) rot=(1,0,0;1.5708rad)
  sketch-geometry (4):
    g0: LineSegment StartX=116.29 StartY=22 StartZ=0 EndX=116.29 EndY=14 EndZ=0
    g1: LineSegment StartX=116.29 StartY=14 StartZ=0 EndX=108.29 EndY=14 EndZ=0
    g2: LineSegment StartX=108.29 StartY=14 StartZ=0 EndX=111.281 EndY=19.1239 EndZ=0
    g3: ArcOfCircle CenterX=116.29 CenterY=16.2 CenterZ=0 NormalX=0 NormalY=0 NormalZ=1 AngleXU=0 Radius=5.8 StartAngle=1.5708 EndAngle=2.61323
  constraints (10):
    c: Distance(g1) = 8
    c: Coincident(g1,g0)
    c: Coincident(g2,g1)
    c: Coincident(g0,g-4)
    c: Coincident(g0,g-4)
    c: PointOnObject(g1,g-3)
    c: PointOnObject(g3,g0)
    c: Coincident(g3,g0)
    c: Radius(g3) = 5.8
    c: Tangent(g2,g3) = 1.5708
FEATURE [PartDesign::Pad] Pad007
  BaseFeature = -> Pocket008
  Direction = (0.707107,-0.707107,0)
  Length = 3
  Length2 = 10
  Profile = -> Sketch011
  ReferenceAxis = -> Sketch011 [N_Axis]
  Refine = true
  Reversed = true
  Suppressed = false
  Type = 0
FEATURE [PartDesign::Pad] Pad008
  BaseFeature = -> Pad007
  Direction = (-3.9e-15,-1,2e-16)
  Length = 3
  Length2 = 10
  Profile = -> Sketch012
  ReferenceAxis = -> Sketch012 [N_Axis]
  Refine = true
  Reversed = true
  Suppressed = false
  Type = 0
FEATURE [PartDesign::Pocket] Pocket009
  BaseFeature = -> Pad008
  Direction = (0,0,1)
  Length = 5
  Length2 = 5
  Profile = -> Binder003
  Refine = true
  Suppressed = false
  Type = 1
FEATURE [Sketcher::SketchObject] Sketch013
  ArcFitTolerance = 1e-06
  AttachmentSupport = -> [Pocket009]
  ExternalGeometry = -> [Pocket009]
  FullyConstrained = true
  MakeInternals = false
  MapMode = 5
  Placement = pos=(0,0,12) rot=(0,0,1;0rad)
  sketch-geometry (6):
    g0: Circle CenterX=64.1715 CenterY=70.175 CenterZ=0 NormalX=0 NormalY=0 NormalZ=1 AngleXU=0 Radius=2.05
    g1: Circle CenterX=143.726 CenterY=57.675 CenterZ=0 NormalX=0 NormalY=0 NormalZ=1 AngleXU=0 Radius=2.05
    g2: Circle CenterX=143.726 CenterY=0.525 CenterZ=0 NormalX=0 NormalY=0 NormalZ=1 AngleXU=0 Radius=2.05
    g3: Circle CenterX=121.033 CenterY=-10.1679 CenterZ=0 NormalX=0 NormalY=0 NormalZ=1 AngleXU=0 Radius=2.05
    g4: Circle CenterX=76.8847 CenterY=-7.82676 CenterZ=0 NormalX=0 NormalY=0 NormalZ=1 AngleXU=0 Radius=2.05
    g5: Circle CenterX=33.1742 CenterY=-25.9322 CenterZ=0 NormalX=0 NormalY=0 NormalZ=1 AngleXU=0 Radius=2.05
  constraints (12):
    c: Coincident(g0,g-3)
    c: Coincident(g1,g-4)
    c: Coincident(g2,g-5)
    c: Coincident(g3,g-6)
    c: Coincident(g4,g-7)
    c: Coincident(g5,g-8)
    c: Diameter(g0) = 4.1
    c: Equal(g0,g1)
    c: Equal(g1,g2)
    c: Equal(g2,g3)
    c: Equal(g3,g4)
    c: Equal(g4,g5)
FEATURE [PartDesign::Pocket] Pocket010
  BaseFeature = -> Pocket009
  Direction = (0,0,-1)
  Length = 1.2
  Length2 = 5
  Profile = -> Sketch013
  ReferenceAxis = -> Sketch013 [N_Axis]
  Refine = true
  Suppressed = false
  Type = 0
FEATURE [Sketcher::SketchObject] Sketch014
  ArcFitTolerance = 1e-06
  AttachmentSupport = -> [Pocket010]
  ExternalGeometry = -> [Pocket010]
  FullyConstrained = true
  MakeInternals = false
  MapMode = 5
  Placement = pos=(0,0,9) rot=(1,0,0;3.14159rad)
  sketch-geometry (124):
    g0: LineSegment StartX=55.5006 StartY=7.5 StartZ=0 EndX=55.5006 EndY=-7.5 EndZ=0
    g1: LineSegment StartX=55.5006 StartY=-7.5 StartZ=0 EndX=60.5006 EndY=-7.5 EndZ=0
    g2: LineSegment StartX=60.5006 StartY=-7.5 StartZ=0 EndX=60.5006 EndY=7.5 EndZ=0
    g3: LineSegment StartX=60.5006 StartY=7.5 StartZ=0 EndX=55.5006 EndY=7.5 EndZ=0
    g4: LineSegment StartX=32.4374 StartY=5.79596 StartZ=0 EndX=39.9374 EndY=18.7863 EndZ=0
    g5: LineSegment StartX=39.9374 StartY=18.7863 StartZ=0 EndX=44.2675 EndY=16.2863 EndZ=0
    g6: LineSegment StartX=44.2675 StartY=16.2863 StartZ=0 EndX=36.7675 EndY=3.29596 EndZ=0
    g7: LineSegment StartX=36.7675 StartY=3.29596 StartZ=0 EndX=32.4374 EndY=5.79596 EndZ=0
    g8: LineSegment StartX=49.4624 StartY=35.2841 StartZ=0 EndX=41.9624 EndY=22.2937 EndZ=0
    g9: LineSegment StartX=41.9624 StartY=22.2937 StartZ=0 EndX=46.2925 EndY=19.7937 EndZ=0
    g10: LineSegment StartX=46.2925 StartY=19.7937 StartZ=0 EndX=53.7925 EndY=32.7841 EndZ=0
    g11: LineSegment StartX=53.7925 StartY=32.7841 StartZ=0 EndX=49.4624 EndY=35.2841 EndZ=0
    g12: LineSegment StartX=20.9858 StartY=34.151 StartZ=0 EndX=10.3792 EndY=23.5444 EndZ=0
    g13: LineSegment StartX=10.3792 StartY=23.5444 StartZ=0 EndX=13.9147 EndY=20.0089 EndZ=0
    g14: LineSegment StartX=13.9147 StartY=20.0089 StartZ=0 EndX=24.5214 EndY=30.6155 EndZ=0
    g15: LineSegment StartX=24.5214 StartY=30.6155 StartZ=0 EndX=20.9858 EndY=34.151 EndZ=0
    g16: LineSegment StartX=34.4562 StartY=47.6214 StartZ=0 EndX=23.8496 EndY=37.0148 EndZ=0
    g17: LineSegment StartX=23.8496 StartY=37.0148 StartZ=0 EndX=27.3851 EndY=33.4793 EndZ=0
    g18: LineSegment StartX=27.3851 StartY=33.4793 StartZ=0 EndX=37.9917 EndY=44.0859 EndZ=0
    g19: LineSegment StartX=37.9917 StartY=44.0859 StartZ=0 EndX=34.4562 EndY=47.6214 EndZ=0
    g20: LineSegment StartX=67.1504 StartY=27.2511 StartZ=0 EndX=63.2681 EndY=12.7622 EndZ=0
    g21: LineSegment StartX=63.2681 StartY=12.7622 StartZ=0 EndX=68.0977 EndY=11.4681 EndZ=0
    g22: LineSegment StartX=68.0977 StartY=11.4681 StartZ=0 EndX=71.98 EndY=25.957 EndZ=0
    g23: LineSegment StartX=71.98 StartY=25.957 StartZ=0 EndX=67.1504 EndY=27.2511 EndZ=0
    g24: LineSegment StartX=86.3147 StartY=24.0698 StartZ=0 EndX=86.3147 EndY=9.06983 EndZ=0
    g25: LineSegment StartX=86.3147 StartY=9.06983 StartZ=0 EndX=91.3147 EndY=9.06983 EndZ=0
    g26: LineSegment StartX=91.3147 StartY=9.06983 StartZ=0 EndX=91.3147 EndY=24.0698 EndZ=0
    g27: LineSegment StartX=91.3147 StartY=24.0698 StartZ=0 EndX=86.3147 EndY=24.0698 EndZ=0
    g28: LineSegment StartX=105.365 StartY=24.0698 StartZ=0 EndX=105.365 EndY=9.06983 EndZ=0
    g29: LineSegment StartX=105.365 StartY=9.06983 StartZ=0 EndX=110.365 EndY=9.06983 EndZ=0
    g30: LineSegment StartX=110.365 StartY=9.06983 StartZ=0 EndX=110.365 EndY=24.0698 EndZ=0
    g31: LineSegment StartX=110.365 StartY=24.0698 StartZ=0 EndX=105.365 EndY=24.0698 EndZ=0
    g32: LineSegment StartX=131.701 StartY=16.5 StartZ=0 EndX=131.701 EndY=1.5 EndZ=0
    g33: LineSegment StartX=131.701 StartY=1.5 StartZ=0 EndX=136.701 EndY=1.5 EndZ=0
    g34: LineSegment StartX=136.701 StartY=1.5 StartZ=0 EndX=136.701 EndY=16.5 EndZ=0
    g35: LineSegment StartX=136.701 StartY=16.5 StartZ=0 EndX=131.701 EndY=16.5 EndZ=0
    g36: LineSegment StartX=150.751 StartY=16.5 StartZ=0 EndX=150.751 EndY=1.5 EndZ=0
    g37: LineSegment StartX=150.751 StartY=1.5 StartZ=0 EndX=155.751 EndY=1.5 EndZ=0
    g38: LineSegment StartX=155.751 StartY=1.5 StartZ=0 EndX=155.751 EndY=16.5 EndZ=0
    g39: LineSegment StartX=155.751 StartY=16.5 StartZ=0 EndX=150.751 EndY=16.5 EndZ=0
    g40: LineSegment StartX=150.751 StartY=-2.55 StartZ=0 EndX=150.751 EndY=-17.55 EndZ=0
    g41: LineSegment StartX=150.751 StartY=-17.55 StartZ=0 EndX=155.751 EndY=-17.55 EndZ=0
    g42: LineSegment StartX=155.751 StartY=-17.55 StartZ=0 EndX=155.751 EndY=-2.55 EndZ=0
    g43: LineSegment StartX=155.751 StartY=-2.55 StartZ=0 EndX=150.751 EndY=-2.55 EndZ=0
    g44: LineSegment StartX=150.751 StartY=-21.6 StartZ=0 EndX=150.751 EndY=-36.6 EndZ=0
    g45: LineSegment StartX=150.751 StartY=-36.6 StartZ=0 EndX=155.751 EndY=-36.6 EndZ=0
    g46: LineSegment StartX=155.751 StartY=-36.6 StartZ=0 EndX=155.751 EndY=-21.6 EndZ=0
    g47: LineSegment StartX=155.751 StartY=-21.6 StartZ=0 EndX=150.751 EndY=-21.6 EndZ=0
    g48: LineSegment StartX=150.751 StartY=-40.65 StartZ=0 EndX=150.751 EndY=-55.65 EndZ=0
    g49: LineSegment StartX=150.751 StartY=-55.65 StartZ=0 EndX=155.751 EndY=-55.65 EndZ=0
    g50: LineSegment StartX=155.751 StartY=-55.65 StartZ=0 EndX=155.751 EndY=-40.65 EndZ=0
    g51: LineSegment StartX=155.751 StartY=-40.65 StartZ=0 EndX=150.751 EndY=-40.65 EndZ=0
    g52: LineSegment StartX=131.701 StartY=-40.65 StartZ=0 EndX=131.701 EndY=-55.65 EndZ=0
    g53: LineSegment StartX=131.701 StartY=-55.65 StartZ=0 EndX=136.701 EndY=-55.65 EndZ=0
    g54: LineSegment StartX=136.701 StartY=-55.65 StartZ=0 EndX=136.701 EndY=-40.65 EndZ=0
    g55: LineSegment StartX=136.701 StartY=-40.65 StartZ=0 EndX=131.701 EndY=-40.65 EndZ=0
    g56: LineSegment StartX=131.701 StartY=-21.6 StartZ=0 EndX=131.701 EndY=-36.6 EndZ=0
    g57: LineSegment StartX=131.701 StartY=-36.6 StartZ=0 EndX=136.701 EndY=-36.6 EndZ=0
    g58: LineSegment StartX=136.701 StartY=-36.6 StartZ=0 EndX=136.701 EndY=-21.6 EndZ=0
    g59: LineSegment StartX=136.701 StartY=-21.6 StartZ=0 EndX=131.701 EndY=-21.6 EndZ=0
    g60: LineSegment StartX=131.701 StartY=-2.55 StartZ=0 EndX=131.701 EndY=-17.55 EndZ=0
    g61: LineSegment StartX=131.701 StartY=-17.55 StartZ=0 EndX=136.701 EndY=-17.55 EndZ=0
    g62: LineSegment StartX=136.701 StartY=-17.55 StartZ=0 EndX=136.701 EndY=-2.55 EndZ=0
    g63: LineSegment StartX=136.701 StartY=-2.55 StartZ=0 EndX=131.701 EndY=-2.55 EndZ=0
    g64: LineSegment StartX=112.651 StartY=4.5 StartZ=0 EndX=112.651 EndY=-10.5 EndZ=0
    g65: LineSegment StartX=112.651 StartY=-10.5 StartZ=0 EndX=117.651 EndY=-10.5 EndZ=0
    g66: LineSegment StartX=117.651 StartY=-10.5 StartZ=0 EndX=117.651 EndY=4.5 EndZ=0
    g67: LineSegment StartX=117.651 StartY=4.5 StartZ=0 EndX=112.651 EndY=4.5 EndZ=0
    g68: LineSegment StartX=93.6006 StartY=-1.5 StartZ=0 EndX=93.6006 EndY=-16.5 EndZ=0
    g69: LineSegment StartX=93.6006 StartY=-16.5 StartZ=0 EndX=98.6006 EndY=-16.5 EndZ=0
    g70: LineSegment StartX=98.6006 StartY=-16.5 StartZ=0 EndX=98.6006 EndY=-1.5 EndZ=0
    g71: LineSegment StartX=98.6006 StartY=-1.5 StartZ=0 EndX=93.6006 EndY=-1.5 EndZ=0
    g72: LineSegment StartX=112.651 StartY=-14.55 StartZ=0 EndX=112.651 EndY=-29.55 EndZ=0
    g73: LineSegment StartX=112.651 StartY=-29.55 StartZ=0 EndX=117.651 EndY=-29.55 EndZ=0
    g74: LineSegment StartX=117.651 StartY=-29.55 StartZ=0 EndX=117.651 EndY=-14.55 EndZ=0
    g75: LineSegment StartX=117.651 StartY=-14.55 StartZ=0 EndX=112.651 EndY=-14.55 EndZ=0
    g76: LineSegment StartX=112.651 StartY=-33.6 StartZ=0 EndX=112.651 EndY=-48.6 EndZ=0
    g77: LineSegment StartX=112.651 StartY=-48.6 StartZ=0 EndX=117.651 EndY=-48.6 EndZ=0
    g78: LineSegment StartX=117.651 StartY=-48.6 StartZ=0 EndX=117.651 EndY=-33.6 EndZ=0
    g79: LineSegment StartX=117.651 StartY=-33.6 StartZ=0 EndX=112.651 EndY=-33.6 EndZ=0
    g80: LineSegment StartX=112.651 StartY=-52.65 StartZ=0 EndX=112.651 EndY=-67.65 EndZ=0
    g81: LineSegment StartX=112.651 StartY=-67.65 StartZ=0 EndX=117.651 EndY=-67.65 EndZ=0
    g82: LineSegment StartX=117.651 StartY=-67.65 StartZ=0 EndX=117.651 EndY=-52.65 EndZ=0
    g83: LineSegment StartX=117.651 StartY=-52.65 StartZ=0 EndX=112.651 EndY=-52.65 EndZ=0
    g84: LineSegment StartX=93.6006 StartY=-20.55 StartZ=0 EndX=93.6006 EndY=-35.55 EndZ=0
    g85: LineSegment StartX=93.6006 StartY=-35.55 StartZ=0 EndX=98.6006 EndY=-35.55 EndZ=0
    g86: LineSegment StartX=98.6006 StartY=-35.55 StartZ=0 EndX=98.6006 EndY=-20.55 EndZ=0
    g87: LineSegment StartX=98.6006 StartY=-20.55 StartZ=0 EndX=93.6006 EndY=-20.55 EndZ=0
    g88: LineSegment StartX=74.5506 StartY=5 StartZ=0 EndX=74.5506 EndY=-10 EndZ=0
    g89: LineSegment StartX=74.5506 StartY=-10 StartZ=0 EndX=79.5506 EndY=-10 EndZ=0
    g90: LineSegment StartX=79.5506 StartY=-10 StartZ=0 EndX=79.5506 EndY=5 EndZ=0
    g91: LineSegment StartX=79.5506 StartY=5 StartZ=0 EndX=74.5506 EndY=5 EndZ=0
    g92: LineSegment StartX=93.6006 StartY=-39.6 StartZ=0 EndX=93.6006 EndY=-54.6 EndZ=0
    g93: LineSegment StartX=93.6006 StartY=-54.6 StartZ=0 EndX=98.6006 EndY=-54.6 EndZ=0
    g94: LineSegment StartX=98.6006 StartY=-54.6 StartZ=0 EndX=98.6006 EndY=-39.6 EndZ=0
    g95: LineSegment StartX=98.6006 StartY=-39.6 StartZ=0 EndX=93.6006 EndY=-39.6 EndZ=0
    g96: LineSegment StartX=93.6006 StartY=-58.65 StartZ=0 EndX=93.6006 EndY=-73.65 EndZ=0
    g97: LineSegment StartX=93.6006 StartY=-73.65 StartZ=0 EndX=98.6006 EndY=-73.65 EndZ=0
    g98: LineSegment StartX=98.6006 StartY=-73.65 StartZ=0 EndX=98.6006 EndY=-58.65 EndZ=0
    g99: LineSegment StartX=98.6006 StartY=-58.65 StartZ=0 EndX=93.6006 EndY=-58.65 EndZ=0
    g100: LineSegment StartX=74.5506 StartY=-52.15 StartZ=0 EndX=74.5506 EndY=-67.15 EndZ=0
    g101: LineSegment StartX=74.5506 StartY=-67.15 StartZ=0 EndX=79.5506 EndY=-67.15 EndZ=0
    g102: LineSegment StartX=79.5506 StartY=-67.15 StartZ=0 EndX=79.5506 EndY=-52.15 EndZ=0
    g103: LineSegment StartX=79.5506 StartY=-52.15 StartZ=0 EndX=74.5506 EndY=-52.15 EndZ=0
    g104: LineSegment StartX=55.5006 StartY=-49.65 StartZ=0 EndX=55.5006 EndY=-64.65 EndZ=0
    g105: LineSegment StartX=55.5006 StartY=-64.65 StartZ=0 EndX=60.5006 EndY=-64.65 EndZ=0
    g106: LineSegment StartX=60.5006 StartY=-64.65 StartZ=0 EndX=60.5006 EndY=-49.65 EndZ=0
    g107: LineSegment StartX=60.5006 StartY=-49.65 StartZ=0 EndX=55.5006 EndY=-49.65 EndZ=0
    g108: LineSegment StartX=55.5006 StartY=-30.6 StartZ=0 EndX=55.5006 EndY=-45.6 EndZ=0
    g109: LineSegment StartX=55.5006 StartY=-45.6 StartZ=0 EndX=60.5006 EndY=-45.6 EndZ=0
    g110: LineSegment StartX=60.5006 StartY=-45.6 StartZ=0 EndX=60.5006 EndY=-30.6 EndZ=0
    g111: LineSegment StartX=60.5006 StartY=-30.6 StartZ=0 EndX=55.5006 EndY=-30.6 EndZ=0
    g112: LineSegment StartX=55.5006 StartY=-11.55 StartZ=0 EndX=55.5006 EndY=-26.55 EndZ=0
    g113: LineSegment StartX=55.5006 StartY=-26.55 StartZ=0 EndX=60.5006 EndY=-26.55 EndZ=0
    g114: LineSegment StartX=60.5006 StartY=-26.55 StartZ=0 EndX=60.5006 EndY=-11.55 EndZ=0
    g115: LineSegment StartX=60.5006 StartY=-11.55 StartZ=0 EndX=55.5006 EndY=-11.55 EndZ=0
    g116: LineSegment StartX=74.5506 StartY=-14.05 StartZ=0 EndX=74.5506 EndY=-29.05 EndZ=0
    g117: LineSegment StartX=74.5506 StartY=-29.05 StartZ=0 EndX=79.5506 EndY=-29.05 EndZ=0
    g118: LineSegment StartX=79.5506 StartY=-29.05 StartZ=0 EndX=79.5506 EndY=-14.05 EndZ=0
    g119: LineSegment StartX=79.5506 StartY=-14.05 StartZ=0 EndX=74.5506 EndY=-14.05 EndZ=0
    g120: LineSegment StartX=74.5506 StartY=-33.1 StartZ=0 EndX=74.5506 EndY=-48.1 EndZ=0
    g121: LineSegment StartX=74.5506 StartY=-48.1 StartZ=0 EndX=79.5506 EndY=-48.1 EndZ=0
    g122: LineSegment StartX=79.5506 StartY=-48.1 StartZ=0 EndX=79.5506 EndY=-33.1 EndZ=0
    g123: LineSegment StartX=79.5506 StartY=-33.1 StartZ=0 EndX=74.5506 EndY=-33.1 EndZ=0
  constraints (372):
    c: Coincident(g0,g1)
    c: Coincident(g1,g2)
    c: Coincident(g2,g3)
    c: Coincident(g3,g0)
    c: Vertical(g0)
    c: Vertical(g2)
    c: Horizontal(g1)
    c: Horizontal(g3)
    c: Distance(g-17,g3) = 0.5
    c: Distance(g-18,g1) = 0.5
    c: DistanceX(g3,g3) = 5
    c: Distance(g-17,g0) = 4.5
    c: Coincident(g5,g4)
    c: Coincident(g6,g5)
    c: Coincident(g4,g7)
    c: Coincident(g6,g7)
    c: Parallel(g7,g-10)
    c: Parallel(g5,g-9)
    c: Perpendicular(g6,g5)
    c: Perpendicular(g4,g7)
    c: Distance(g5,g5) = 5
    c: Distance(g-9,g4) = 4.5
    c: Distance(g-10,g7) = 0.5
    c: Distance(g-9,g5) = 0.5
    c: Coincident(g9,g8)
    c: Coincident(g10,g9)
    c: Coincident(g11,g10)
    c: Coincident(g11,g8)
    c: Distance(g11,g11) = 5
    c: Perpendicular(g9,g8)
    c: Parallel(g9,g-8)
    c: Parallel(g-7,g11)
    c: Perpendicular(g11,g10)
    c: Distance(g-8,g9) = 0.5
    c: Distance(g-7,g11) = 0.5
    c: Distance(g-8,g8) = 4.5
    c: Coincident(g13,g12)
    c: Coincident(g14,g13)
    c: Coincident(g15,g14)
    c: Coincident(g15,g12)
    c: Distance(g13,g13) = 5
    c: Perpendicular(g13,g12)
    c: Parallel(g13,g-6)
    c: Parallel(g-5,g15)
    c: Perpendicular(g15,g14)
    c: Distance(g-5,g12) = 4.5
    c: Distance(g-6,g13) = 0.5
    c: Distance(g-5,g15) = 0.5
    c: Coincident(g17,g16)
    c: Coincident(g18,g17)
    c: Coincident(g19,g18)
    c: Coincident(g19,g16)
    c: Perpendicular(g19,g16)
    c: Perpendicular(g17,g18)
    c: Parallel(g19,g-3)
    c: Parallel(g17,g-4)
    c: Distance(g-3,g19) = 0.5
    c: Distance(g-4,g18) = 4.5
    c: Distance(g17,g17) = 5
    c: Distance(g-4,g17) = 0.5
    c: Coincident(g21,g20)
    c: Coincident(g22,g21)
    c: Coincident(g23,g22)
    c: Coincident(g23,g20)
    c: Parallel(g23,g-11)
    c: Parallel(g21,g-12)
    c: Distance(g-11,g20) = 4.5
    c: Perpendicular(g21,g20)
    c: Perpendicular(g22,g23)
    c: Distance(g23,g23) = 5
    c: Distance(g-11,g23) = 0.5
    c: Distance(g-12,g21) = 0.5
    c: Coincident(g24,g25)
    c: Coincident(g25,g26)
    c: Coincident(g26,g27)
    c: Coincident(g27,g24)
    c: Vertical(g24)
    c: Vertical(g26)
    c: Horizontal(g25)
    c: Horizontal(g27)
    c: Coincident(g28,g29)
    c: Coincident(g29,g30)
    c: Coincident(g30,g31)
    c: Coincident(g31,g28)
    c: Vertical(g28)
    c: Vertical(g30)
    c: Horizontal(g29)
    c: Horizontal(g31)
    c: Coincident(g32,g33)
    c: Coincident(g33,g34)
    c: Coincident(g34,g35)
    c: Coincident(g35,g32)
    c: Vertical(g32)
    c: Vertical(g34)
    c: Horizontal(g33)
    c: Horizontal(g35)
    c: Coincident(g36,g37)
    c: Coincident(g37,g38)
    c: Coincident(g38,g39)
    c: Coincident(g39,g36)
    c: Vertical(g36)
    c: Vertical(g38)
    c: Horizontal(g37)
    c: Horizontal(g39)
    c: Coincident(g40,g41)
    c: Coincident(g41,g42)
    c: Coincident(g42,g43)
    c: Coincident(g43,g40)
    c: Vertical(g40)
    c: Vertical(g42)
    c: Horizontal(g41)
    c: Horizontal(g43)
    c: Coincident(g44,g45)
    c: Coincident(g45,g46)
    c: Coincident(g46,g47)
    c: Coincident(g47,g44)
    c: Vertical(g44)
    c: Vertical(g46)
    c: Horizontal(g45)
    c: Horizontal(g47)
    c: Coincident(g48,g49)
    c: Coincident(g49,g50)
    c: Coincident(g50,g51)
    c: Coincident(g51,g48)
    c: Vertical(g48)
    c: Vertical(g50)
    c: Horizontal(g49)
    c: Horizontal(g51)
    c: Coincident(g52,g53)
    c: Coincident(g53,g54)
    c: Coincident(g54,g55)
    c: Coincident(g55,g52)
    c: Vertical(g52)
    c: Vertical(g54)
    c: Horizontal(g53)
    c: Horizontal(g55)
    c: Coincident(g56,g57)
    c: Coincident(g57,g58)
    c: Coincident(g58,g59)
    c: Coincident(g59,g56)
    c: Vertical(g56)
    c: Vertical(g58)
    c: Horizontal(g57)
    c: Horizontal(g59)
    c: Coincident(g60,g61)
    c: Coincident(g61,g62)
    c: Coincident(g62,g63)
    c: Coincident(g63,g60)
    c: Vertical(g60)
    c: Vertical(g62)
    c: Horizontal(g61)
    c: Horizontal(g63)
    c: Coincident(g64,g65)
    c: Coincident(g65,g66)
    c: Coincident(g66,g67)
    c: Coincident(g67,g64)
    c: Vertical(g64)
    c: Vertical(g66)
    c: Horizontal(g65)
    c: Horizontal(g67)
    c: Coincident(g68,g69)
    c: Coincident(g69,g70)
    c: Coincident(g70,g71)
    c: Coincident(g71,g68)
    c: Vertical(g68)
    c: Vertical(g70)
    c: Horizontal(g69)
    c: Horizontal(g71)
    c: Coincident(g72,g73)
    c: Coincident(g73,g74)
    c: Coincident(g74,g75)
    c: Coincident(g75,g72)
    c: Vertical(g72)
    c: Vertical(g74)
    c: Horizontal(g73)
    c: Horizontal(g75)
    c: Coincident(g76,g77)
    c: Coincident(g77,g78)
    c: Coincident(g78,g79)
    c: Coincident(g79,g76)
    c: Vertical(g76)
    c: Vertical(g78)
    c: Horizontal(g77)
    c: Horizontal(g79)
    c: Coincident(g80,g81)
    c: Coincident(g81,g82)
    c: Coincident(g82,g83)
    c: Coincident(g83,g80)
    c: Vertical(g80)
    c: Vertical(g82)
    c: Horizontal(g81)
    c: Horizontal(g83)
    c: Coincident(g84,g85)
    c: Coincident(g85,g86)
    c: Coincident(g86,g87)
    c: Coincident(g87,g84)
    c: Vertical(g84)
    c: Vertical(g86)
    c: Horizontal(g85)
    c: Horizontal(g87)
    c: Coincident(g88,g89)
    c: Coincident(g89,g90)
    c: Coincident(g90,g91)
    c: Coincident(g91,g88)
    c: Vertical(g88)
    c: Vertical(g90)
    c: Horizontal(g89)
    c: Horizontal(g91)
    c: Coincident(g92,g93)
    c: Coincident(g93,g94)
    c: Coincident(g94,g95)
    c: Coincident(g95,g92)
    c: Vertical(g92)
    c: Vertical(g94)
    c: Horizontal(g93)
    c: Horizontal(g95)
    c: Coincident(g96,g97)
    c: Coincident(g97,g98)
    c: Coincident(g98,g99)
    c: Coincident(g99,g96)
    c: Vertical(g96)
    c: Vertical(g98)
    c: Horizontal(g97)
    c: Horizontal(g99)
    c: Coincident(g100,g101)
    c: Coincident(g101,g102)
    c: Coincident(g102,g103)
    c: Coincident(g103,g100)
    c: Vertical(g100)
    c: Vertical(g102)
    c: Horizontal(g101)
    c: Horizontal(g103)
    c: Coincident(g104,g105)
    c: Coincident(g105,g106)
    c: Coincident(g106,g107)
    c: Coincident(g107,g104)
    c: Vertical(g104)
    c: Vertical(g106)
    c: Horizontal(g105)
    c: Horizontal(g107)
    c: Coincident(g108,g109)
    c: Coincident(g109,g110)
    c: Coincident(g110,g111)
    c: Coincident(g111,g108)
    c: Vertical(g108)
    c: Vertical(g110)
    c: Horizontal(g109)
    c: Horizontal(g111)
    c: Coincident(g112,g113)
    c: Coincident(g113,g114)
    c: Coincident(g114,g115)
    c: Coincident(g115,g112)
    c: Vertical(g112)
    c: Vertical(g114)
    c: Horizontal(g113)
    c: Horizontal(g115)
    c: Coincident(g116,g117)
    c: Coincident(g117,g118)
    c: Coincident(g118,g119)
    c: Coincident(g119,g116)
    c: Vertical(g116)
    c: Vertical(g118)
    c: Horizontal(g117)
    c: Horizontal(g119)
    c: Coincident(g120,g121)
    c: Coincident(g121,g122)
    c: Coincident(g122,g123)
    c: Coincident(g123,g120)
    c: Vertical(g120)
    c: Vertical(g122)
    c: Horizontal(g121)
    c: Horizontal(g123)
    c: DistanceX(g27,g27) = 5
    c: DistanceX(g31,g31) = 5
    c: DistanceX(g35,g35) = 5
    c: DistanceX(g39,g39) = 5
    c: DistanceX(g43,g43) = 5
    c: DistanceX(g47,g47) = 5
    c: DistanceX(g51,g51) = 5
    c: DistanceX(g55,g55) = 5
    c: Distance(g57,g57) = 5
    c: Distance(g61,g61) = 5
    c: Distance(g67,g67) = 5
    c: Distance(g75,g75) = 5
    c: Distance(g79,g79) = 5
    c: Distance(g83,g83) = 5
    c: Distance(g99,g99) = 5
    c: Distance(g95,g95) = 5
    c: Distance(g87,g87) = 5
    c: DistanceX(g71,g71) = 5
    c: Distance(g91,g91) = 5
    c: Distance(g119,g119) = 5
    c: Distance(g123,g123) = 5
    c: Distance(g103,g103) = 5
    c: Distance(g107,g107) = 5
    c: Distance(g111,g111) = 5
    c: Distance(g115,g115) = 5
    c: Distance(g-13,g27) = 0.5
    c: Distance(g-14,g25) = 0.5
    c: Distance(g-15,g31) = 0.5
    c: Distance(g-16,g29) = 0.5
    c: Distance(g-25,g35) = 0.5
    c: Distance(g-26,g33) = 0.5
    c: Distance(g-27,g39) = 0.5
    c: Distance(g-28,g37) = 0.5
    c: Distance(g-29,g43) = 0.5
    c: Distance(g-30,g41) = 0.5
    c: Distance(g-31,g47) = 0.5
    c: Distance(g-32,g45) = 0.5
    c: Distance(g-33,g51) = 0.5
    c: Distance(g-34,g49) = 0.5
    c: Distance(g-36,g53) = 0.5
    c: Distance(g-35,g55) = 0.5
    c: Distance(g-62,g57) = 0.5
    c: Distance(g-61,g59) = 0.5
    c: Distance(g-64,g61) = 0.5
    c: Distance(g63,g-63) = 0.5
    c: Distance(g67,g-23) = 0.5
    c: Distance(g-24,g65) = 0.5
    c: Distance(g75,g-41) = 0.5
    c: Distance(g-42,g73) = 0.5
    c: Distance(g-39,g79) = 0.5
    c: Distance(g-40,g77) = 0.5
    c: Distance(g-38,g81) = 0.5
    c: Distance(g-37,g83) = 0.5
    c: Distance(g-21,g71) = 0.5
    c: Distance(g-22,g69) = 0.5
    c: Distance(g-43,g87) = 0.5
    c: Distance(g-44,g85) = 0.5
    c: Distance(g-59,g95) = 0.5
    c: Distance(g-60,g93) = 0.5
    c: Distance(g-58,g97) = 0.5
    c: Distance(g-57,g99) = 0.5
    c: Distance(g-56,g101) = 0.5
    c: Distance(g-55,g103) = 0.5
    c: Distance(g-52,g121) = 0.5
    c: Distance(g-51,g123) = 0.5
    c: Distance(g-46,g117) = 0.5
    c: Distance(g-45,g119) = 0.5
    c: Distance(g-20,g89) = 0.5
    c: Distance(g-19,g91) = 0.5
    c: Distance(g-47,g115) = 0.5
    c: Distance(g-48,g113) = 0.5
    c: Distance(g111,g-49) = 0.5
    c: Distance(g-50,g109) = 0.5
    c: Distance(g-54,g105) = 0.5
    c: Distance(g-14,g24) = 4.5
    c: Distance(g-16,g28) = 4.5
    c: Distance(g-25,g32) = 4.5
    c: Distance(g-28,g36) = 4.5
    c: Distance(g-29,g40) = 4.5
    c: DistanceX(g-31,g44) = 4.5
    c: Distance(g-33,g48) = 4.5
    c: Distance(g-63,g60) = 4.5
    c: Distance(g-61,g56) = 4.5
    c: Distance(g-35,g52) = 4.5
    c: Distance(g-23,g64) = 4.5
    c: Distance(g-41,g74) = 4.5
    c: Distance(g-39,g78) = 4.5
    c: Distance(g-37,g82) = 4.5
    c: Distance(g-57,g98) = 4.5
    c: Distance(g-59,g94) = 4.5
    c: Distance(g-43,g86) = 4.5
    c: Distance(g-21,g70) = 4.5
    c: Distance(g-19,g88) = 4.5
    c: Distance(g-45,g118) = 4.5
    c: Distance(g-51,g120) = 4.5
    c: Distance(g-55,g100) = 4.5
    c: Distance(g-53,g104) = 4.5
    c: Distance(g-53,g107) = 0.5
    c: Distance(g-49,g108) = 4.5
    c: Distance(g-47,g112) = 4.5
FEATURE [PartDesign::Pocket] Pocket011
  BaseFeature = -> Pocket010
  Direction = (0,0,1)
  Length = 1.4
  Length2 = 5
  Profile = -> Sketch014
  ReferenceAxis = -> Sketch014 [N_Axis]
  Refine = true
  Suppressed = false
  Type = 0
FEATURE [PartDesign::Chamfer] Chamfer
  Angle = 45
  Base = -> Pocket011 [Edge274,Edge261,Edge37,Edge10,Edge8,Edge7,Edge6,Edge23,Edge28,Edge245,Edge284,Edge283,Edge282,Edge281,Edge280,Edge279,Edge278,Edge277,Edge276,Edge275,Edge26,Edge243,Edge242,Edge241,Edge942,Edge1012,Edge1004,Edge1010,Edge1003,Edge990,Edge1000,Edge989,Edge972,Edge986,Edge971,Edge969,Edge949,Edge251,Edge250,Edge33]
  BaseFeature = -> Pocket011
  ChamferType = 0
  FlipDirection = false
  Refine = true
  Size = 1.5
  Size2 = 1
  SupportTransform = false
  Suppressed = false
  UseAllEdges = false
FEATURE [PartDesign::Body] Body
  AllowCompound = false
  Group = -> [Sketch,Pad,Sketch002,Sketch003,Sketch004,Sketch005,Sketch006,Sketch007,Sketch008,Sketch009,Sketch015,Pad009,Pocket,Pocket001,Pocket002,Pocket003,Pocket004,Pocket005,Pocket006,Pocket007,Sketch010,Pocket008,Sketch011,Sketch012,Pad007,Pad008,Binder003,Pocket009,Sketch013,Pocket010,Sketch014,Pocket011,Chamfer]
  Origin = -> Origin
  Tip = -> Chamfer
